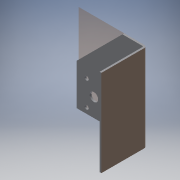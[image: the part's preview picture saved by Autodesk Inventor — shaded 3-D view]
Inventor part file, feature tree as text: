
AUTODESK INVENTOR PART (.ipt)
format: ipt  version: 2019 (Build 230136000, 136)  size: 129,024 bytes
history: native  units: mm
features: sketch x3, hole x2, thicken_offset x1, chamfer x1, other x1, extrude x1
ambient origin geometry x8: Origin, YZ Plane, XZ Plane, XY Plane, X Axis, Y Axis, Z Axis, Center Point
bodies: Solid1 (feature_tree)
feature tree (9):
  thicken_offset  "Thicken1"
  hole  "Hole1"  [1 undecoded]
  hole  "Hole2"  [1 undecoded]
  chamfer  "Chamfer1"  Distance=3.2mm
  sketch  "Sketch1"  dims[d0=120.0mm d1=80.0mm]
  other  "Srf1"
  sketch  "Sketch2"  dims[d2=5.0mm d3=150.0mm d4=0.0mm]
  sketch  "Sketch3"  dims[d5=3.2mm d6=3.2mm d7=15.0mm d8=6.0mm d9=4.0mm d10=2.0mm d11=90.0deg d12=22.2mm d13=20.594885mm d14=2.0mm d15=0.0mm d16=30.0mm d17=90.0mm d18=7.0mm d19=6.0mm d20=4.0mm d21=2.0mm d22=90.0deg d23=22.2mm d24=20.594885mm d25=0.0mm d26=0.0mm d27=50.8mm d28=120.0deg d29=120.0deg d30=80.0mm d31=2.0mm d32=45.0deg]
  extrude  "ExtrusionSrf1"  Depth=80.0mm TaperAngle=0.0deg
note: 2 required parameter values undecoded (feature->parameter linkage not recoverable at this tier; creation-order binding heuristic only, values carry confidence <= 0.55)
